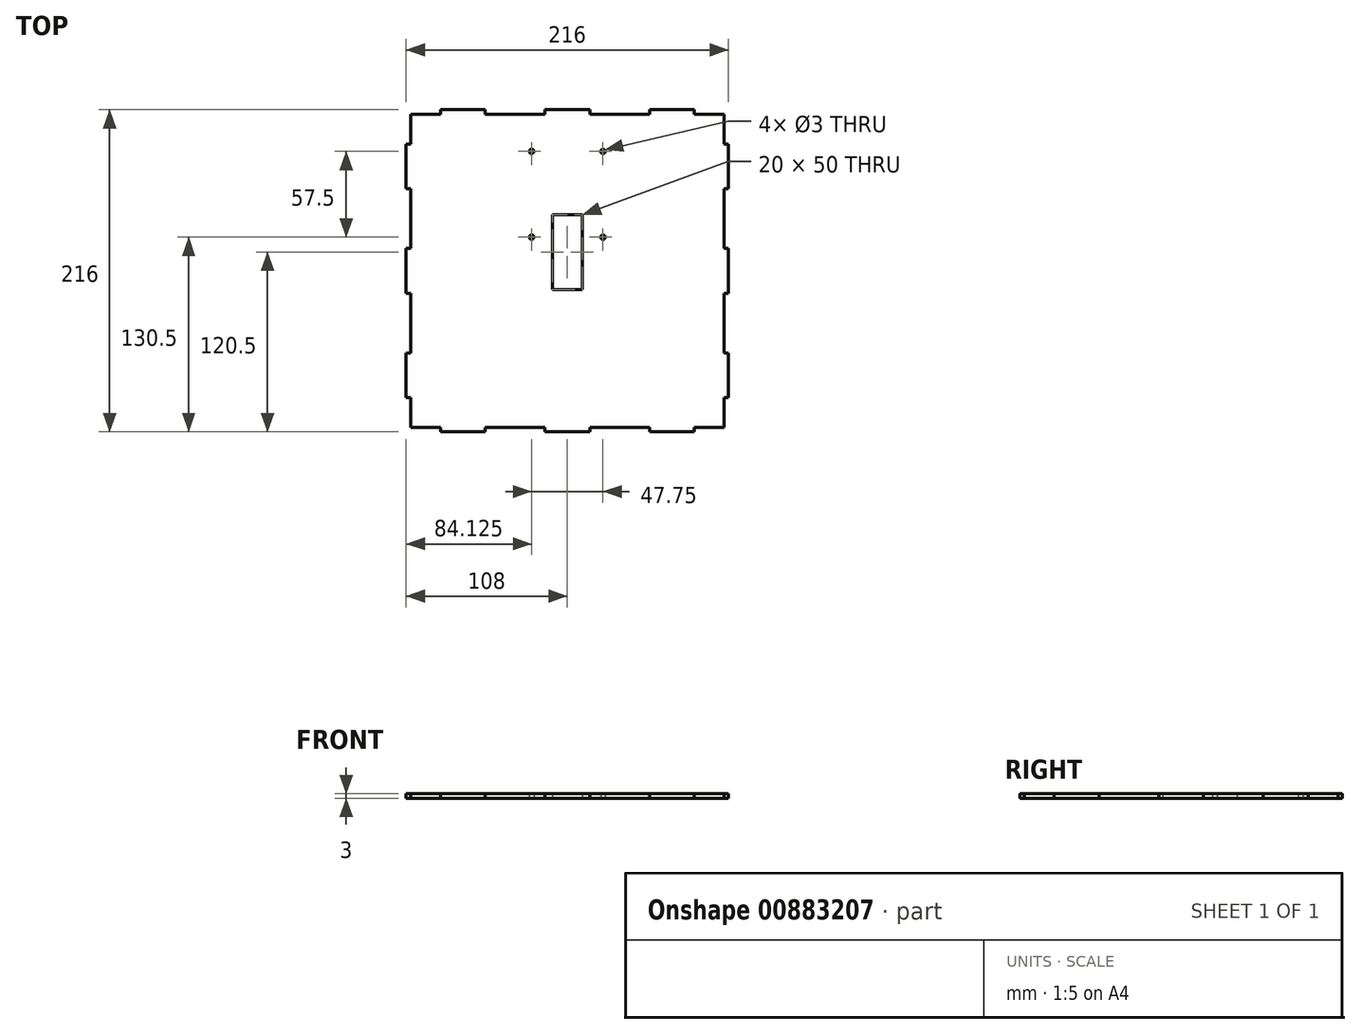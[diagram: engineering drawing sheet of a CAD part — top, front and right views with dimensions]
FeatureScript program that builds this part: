
annotation { "Feature Type Name" : "Feature", "Feature Type Description" : "" }
export const myFeature = defineFeature(function(context is Context, id is Id, definition is map)
    precondition{}
    {
        {
            var Q0;
            Q0=qCreatedBy(makeId("Top.planeOp"),FACE);
            var sketch = newSketch(context, id + "F0", { "sketchPlane" : qUnion([Q0])});
            skLineSegment(sketch, "E0.bottom", {"start": v(0, 0) * mm, "end": v(210, 0) * mm});
            skLineSegment(sketch, "E0.top", {"start": v(0, 210) * mm, "end": v(210, 210) * mm});
            skLineSegment(sketch, "E0.left", {"start": v(0, 0) * mm, "end": v(0, 210) * mm});
            skLineSegment(sketch, "E0.right", {"start": v(210, 0) * mm, "end": v(210, 210) * mm});
            skLineSegment(sketch, "E1", {"start": v(0, 190) * mm, "end": v(-3, 190) * mm});
            skLineSegment(sketch, "E2", {"start": v(-3, 190) * mm, "end": v(-3, 160) * mm});
            skLineSegment(sketch, "E3", {"start": v(-3, 160) * mm, "end": v(0, 160) * mm});
            skLineSegment(sketch, "E4", {"start": v(0, 120) * mm, "end": v(-3, 120) * mm});
            skLineSegment(sketch, "E5", {"start": v(-3, 120) * mm, "end": v(-3, 90) * mm});
            skLineSegment(sketch, "E6", {"start": v(-3, 90) * mm, "end": v(0, 90) * mm});
            skLineSegment(sketch, "E7", {"start": v(0, 50) * mm, "end": v(-3, 50) * mm});
            skLineSegment(sketch, "E8", {"start": v(-3, 50) * mm, "end": v(-3, 20) * mm});
            skLineSegment(sketch, "E9", {"start": v(-3, 20) * mm, "end": v(0, 20) * mm});
            skLineSegment(sketch, "E10", {"start": v(20, 0) * mm, "end": v(20, -3) * mm});
            skLineSegment(sketch, "E11", {"start": v(20, -3) * mm, "end": v(50, -3) * mm});
            skLineSegment(sketch, "E12", {"start": v(50, -3) * mm, "end": v(50, 0) * mm});
            skLineSegment(sketch, "E13", {"start": v(90, 0) * mm, "end": v(90, -3) * mm});
            skLineSegment(sketch, "E14", {"start": v(90, -3) * mm, "end": v(120, -3) * mm});
            skLineSegment(sketch, "E15", {"start": v(120, -3) * mm, "end": v(120, 0) * mm});
            skLineSegment(sketch, "E16", {"start": v(160, 0) * mm, "end": v(160, -3) * mm});
            skLineSegment(sketch, "E17", {"start": v(160, -3) * mm, "end": v(190, -3) * mm});
            skLineSegment(sketch, "E18", {"start": v(190, -3) * mm, "end": v(190, 0) * mm});
            skPoint(sketch, "E19", {"position": v(-3, 105) * mm});
            skPoint(sketch, "E20", {"position": v(0, 105) * mm});
            skPoint(sketch, "E21", {"position": v(105, 0) * mm});
            skPoint(sketch, "E22", {"position": v(105, -3) * mm});
            skLineSegment(sketch, "E23", {"start": v(105, 210) * mm, "end": v(105, 0) * mm, "construction": true});
            skLineSegment(sketch, "E24", {"start": v(0, 105) * mm, "end": v(210, 105) * mm, "construction": true});
            skLineSegment(sketch, "E25.MirrorCS", {"start": v(210, 190) * mm, "end": v(213, 190) * mm});
            skLineSegment(sketch, "E26.MirrorCS", {"start": v(213, 190) * mm, "end": v(213, 160) * mm});
            skLineSegment(sketch, "E27.MirrorCS", {"start": v(213, 160) * mm, "end": v(210, 160) * mm});
            skLineSegment(sketch, "E28.MirrorCS", {"start": v(210, 120) * mm, "end": v(213, 120) * mm});
            skLineSegment(sketch, "E29.MirrorCS", {"start": v(213, 120) * mm, "end": v(213, 90) * mm});
            skLineSegment(sketch, "E30.MirrorCS", {"start": v(213, 90) * mm, "end": v(210, 90) * mm});
            skLineSegment(sketch, "E31.MirrorCS", {"start": v(210, 50) * mm, "end": v(213, 50) * mm});
            skLineSegment(sketch, "E32.MirrorCS", {"start": v(213, 50) * mm, "end": v(213, 20) * mm});
            skLineSegment(sketch, "E33.MirrorCS", {"start": v(213, 20) * mm, "end": v(210, 20) * mm});
            skLineSegment(sketch, "E34.MirrorCS", {"start": v(20, 210) * mm, "end": v(20, 213) * mm});
            skLineSegment(sketch, "E35.MirrorCS", {"start": v(20, 213) * mm, "end": v(50, 213) * mm});
            skLineSegment(sketch, "E36.MirrorCS", {"start": v(50, 213) * mm, "end": v(50, 210) * mm});
            skLineSegment(sketch, "E37.MirrorCS", {"start": v(90, 210) * mm, "end": v(90, 213) * mm});
            skLineSegment(sketch, "E38.MirrorCS", {"start": v(90, 213) * mm, "end": v(120, 213) * mm});
            skLineSegment(sketch, "E39.MirrorCS", {"start": v(120, 213) * mm, "end": v(120, 210) * mm});
            skLineSegment(sketch, "E40.MirrorCS", {"start": v(160, 210) * mm, "end": v(160, 213) * mm});
            skLineSegment(sketch, "E41.MirrorCS", {"start": v(160, 213) * mm, "end": v(190, 213) * mm});
            skLineSegment(sketch, "E42.MirrorCS", {"start": v(190, 213) * mm, "end": v(190, 210) * mm});
            skCircle(sketch, "E43", {"center": v(128.88, 185) * mm, "radius": 1.5 * mm});
            skCircle(sketch, "E44", {"center": v(128.88, 127.5) * mm, "radius": 1.5 * mm});
            skCircle(sketch, "E45.MirrorC", {"center": v(81.12, 185) * mm, "radius": 1.5 * mm});
            skCircle(sketch, "E46.MirrorC", {"center": v(81.12, 127.5) * mm, "radius": 1.5 * mm});
            skLineSegment(sketch, "E47.bottom", {"start": v(95, 142.5) * mm, "end": v(115, 142.5) * mm});
            skLineSegment(sketch, "E47.top", {"start": v(95, 92.5) * mm, "end": v(115, 92.5) * mm});
            skLineSegment(sketch, "E47.left", {"start": v(95, 142.5) * mm, "end": v(95, 92.5) * mm});
            skLineSegment(sketch, "E47.right", {"start": v(115, 142.5) * mm, "end": v(115, 92.5) * mm});
            skPoint(sketch, "E47.middle", {"position": v(105, 127.5) * mm});
            skSolve(sketch);
        }
        {
            var Q0;
            Q0 = qSketchRegion(id + "F0", true);
            extrude(context, id + "F1", {"entities" : qUnion([Q0]), "depth" : 3 * mm, "offsetDistance" : 25 * mm});
        }
    });
